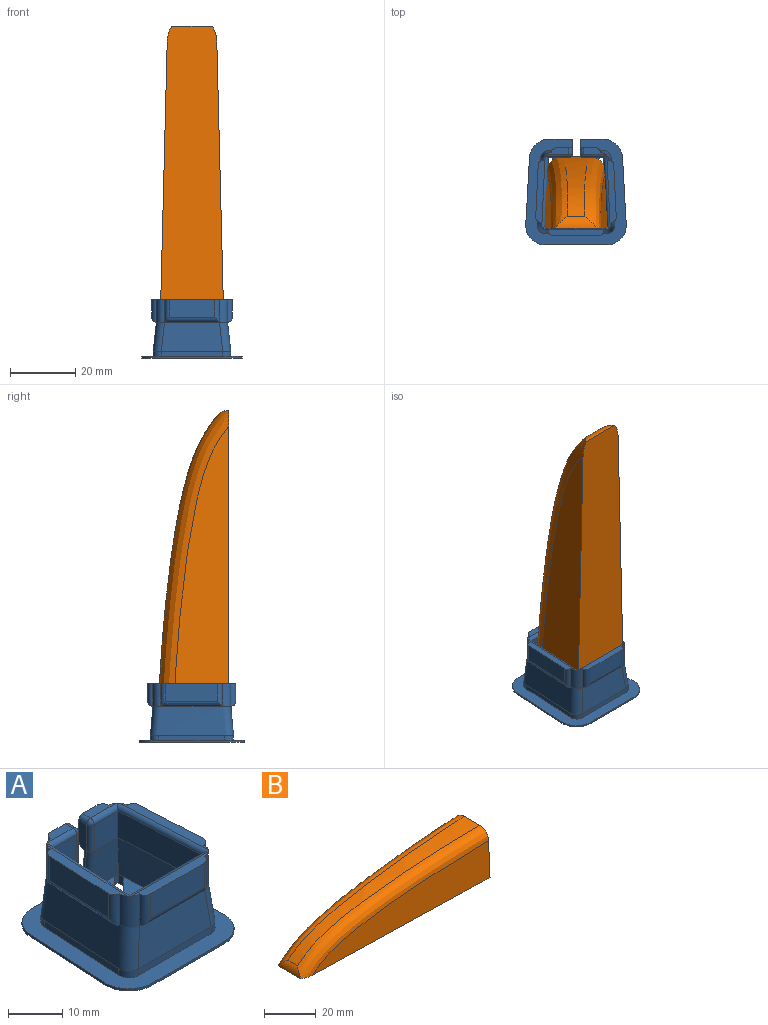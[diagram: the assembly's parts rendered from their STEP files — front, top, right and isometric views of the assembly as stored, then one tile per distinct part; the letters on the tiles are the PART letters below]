
ASSEMBLY  parts=2 mates=1
PART A: 109 faces, bbox 31x32.6x18.1 mm
  f0: plane 6.74x2mm, normal (0,0,1), area 10.5mm2, adj f11,f76,f82,f104,f108
  f1: plane 22x2.9mm, normal (0,0,1), area 38.1mm2, adj f71,f76,f81,f85,f87,f107
  f2: plane 6.85x2mm, normal (0,0,1), area 10.7mm2, adj f69,f78,f84,f97,f100
  f3: plane 22x2.9mm, normal (0,0,1), area 38.1mm2, adj f69,f70,f79,f88,f90,f102
  f4: plane 9.01x6.96mm, normal (0,-1,-0.08), area 59.3mm2, adj f6,f10,f20,f39,f101
  f5: plane 9.01x7.01mm, normal (0,1,0.08), area 59.8mm2, adj f7,f12,f19,f94
  f6: plane 7.07x5.34mm, normal (0,0,1), area 21.4mm2, adj f4,f8,f37,f38,f94,f101
  f7: plane 7.02x1.51mm, normal (0,1,0), area 10.5mm2, adj f5,f24,f68,f94
  f8: cylinder r=2.25mm len=2mm, axis (0,0,-1), area 0.9mm2, adj f6,f37,f59,f94
  f9: plane 7x0.5mm, normal (0,1,0), area 3.5mm2, adj f59,f67,f68,f94
  f10: plane 6.19x6mm, normal (0,-1,0), area 37.2mm2, adj f4,f75,f103,f108
  f11: plane 5.5x4.74mm, normal (0,1,0), area 25.9mm2, adj f0,f12,f82,f94,f104
  f12: cylinder r=1.5mm len=6.24mm, axis (-1,0,0), area 12.9mm2, adj f5,f11,f82,f94
  f13: bspline ~22.5x9mm, area 196.9mm2, adj f14,f18,f21,f32,f52,f73
  f14: plane 9.01x7.07mm, normal (0,-1,-0.08), area 60.3mm2, adj f13,f22,f33,f74,f96
  f15: plane 9.01x7.12mm, normal (0,1,0.08), area 60.8mm2, adj f16,f25,f83,f95
  f16: bspline ~25.5x9mm, area 250mm2, adj f15,f17,f26,f27,f28,f69,f70,f89
  f17: plane 18.9x9.01mm, normal (0,-1,0.09), area 161.7mm2, adj f16,f19,f29,f92
  f18: plane 21.01x9.01mm, normal (0,1,-0.09), area 180.7mm2, adj f13,f20,f23,f47,f51,f72
  f19: bspline ~25.5x9mm, area 250mm2, adj f5,f17,f24,f30,f57,f71,f76,f86
  f20: bspline ~22.5x9mm, area 196.9mm2, adj f4,f18,f40,f46,f58,f75
  f21: plane 20.13x7.07mm, normal (0,0,1), area 87.7mm2, adj f13,f31,f53,f54,f55,f56
  f22: plane 7.18x5.34mm, normal (0,0,1), area 21.8mm2, adj f14,f34,f35,f36,f95,f96
  f23: plane 18.97x4.85mm, normal (0,0,1), area 63.3mm2, adj f18,f48,f49,f50
  f24: cylinder r=2.5mm len=2.5mm, axis (0,0,-1), area 5.7mm2, adj f7,f19,f57,f68
  f25: plane 7.12x1.51mm, normal (0,1,0), area 10.7mm2, adj f15,f26,f68,f95
  f26: cylinder r=2.5mm len=2.5mm, axis (0,0,-1), area 5.7mm2, adj f16,f25,f27,f68
  f27: plane 20.59x1.59mm, normal (-1,0.06,0), area 30.8mm2, adj f16,f26,f28,f68
  f28: cylinder r=2.5mm len=2.64mm, axis (0,0,-1), area 6.1mm2, adj f16,f27,f29,f68
  f29: plane 18.9x1.51mm, normal (0,-1,0), area 28.3mm2, adj f17,f28,f30,f68
  f30: cylinder r=2.5mm len=2.64mm, axis (0,0,-1), area 6.1mm2, adj f19,f29,f57,f68
  f31: plane 4.46x4.36mm, normal (0.72,0.7,0), area 12.5mm2, adj f21,f32,f56,f59
  f32: plane 2.01x1.28mm, normal (1,-0.06,0), area 2.5mm2, adj f13,f31,f33,f59
  f33: plane 2.01x0.93mm, normal (0,-1,0), area 1.8mm2, adj f14,f32,f34,f59
  f34: plane 4.3x4.21mm, normal (-0.71,-0.7,0), area 12mm2, adj f22,f33,f35,f59
  f35: plane 2.51x2mm, normal (0,-1,0), area 5mm2, adj f22,f34,f36,f59
  f36: cylinder r=2.25mm len=2mm, axis (0,0,-1), area 1.1mm2, adj f22,f35,f59,f95
  f37: plane 2.51x2mm, normal (0,-1,0), area 5mm2, adj f6,f8,f38,f59
  f38: plane 4.3x4.21mm, normal (0.71,-0.7,0), area 12mm2, adj f6,f37,f39,f59
  f39: plane 2.01x0.93mm, normal (0,-1,0), area 1.8mm2, adj f4,f38,f40,f59
  f40: plane 2.01x1.28mm, normal (-1,-0.06,0), area 2.5mm2, adj f20,f39,f41,f59
  f41: plane 4.46x4.36mm, normal (-0.72,0.7,0), area 12.5mm2, adj f40,f42,f58,f59
  f42: plane 5.03x2mm, normal (-0.95,0.3,0), area 10.5mm2, adj f41,f43,f58,f59
  f43: plane 4.03x2mm, normal (-1,0,0), area 8.1mm2, adj f42,f44,f58,f59
  f44: plane 2x0.89mm, normal (-0.78,-0.63,0), area 2.3mm2, adj f43,f45,f58,f59
  f45: plane 6.35x5.72mm, normal (-0.67,-0.74,0), area 17.1mm2, adj f44,f46,f58,f59
  f46: plane 2.01x1.12mm, normal (-1,-0.06,0), area 2.2mm2, adj f20,f45,f47,f59
  f47: plane 2.01x1.03mm, normal (0,1,0), area 2mm2, adj f18,f46,f48,f59
  f48: plane 5.91x4.85mm, normal (0.63,0.77,0), area 15.3mm2, adj f23,f47,f49,f59
  f49: plane 7.15x2mm, normal (0,1,0), area 14.3mm2, adj f23,f48,f50,f59
  f50: plane 5.91x4.85mm, normal (-0.63,0.77,0), area 15.3mm2, adj f23,f49,f51,f59
  f51: plane 2.01x1.03mm, normal (0,1,0), area 2mm2, adj f18,f50,f52,f59
  f52: plane 2.01x1.12mm, normal (1,-0.06,0), area 2.2mm2, adj f13,f51,f53,f59
  f53: plane 6.35x5.72mm, normal (0.67,-0.74,0), area 17.1mm2, adj f21,f52,f54,f59
  f54: plane 2x0.89mm, normal (0.78,-0.63,0), area 2.3mm2, adj f21,f53,f55,f59
  f55: plane 4.03x2mm, normal (1,0,0), area 8.1mm2, adj f21,f54,f56,f59
  f56: plane 5.03x2mm, normal (0.95,0.3,0), area 10.5mm2, adj f21,f31,f55,f59
  f57: plane 20.59x1.59mm, normal (1,0.06,0), area 30.8mm2, adj f19,f24,f30,f68
  f58: plane 20.12x7.06mm, normal (0,0,1), area 87.4mm2, adj f20,f41,f42,f43,f44,f45
  f59: plane 32.5x30.89mm, normal (0,0,-1), area 760.5mm2, adj f8,f9,f31,f32,f33,f34,f35,f36
  f60: plane 7.11x0.5mm, normal (0,1,0), area 3.6mm2, adj f59,f61,f68,f95
  f61: cylinder r=6mm len=5.99mm, axis (0,0,-1), area 4.5mm2, adj f59,f60,f62,f68
  f62: plane 20.5x1.14mm, normal (-1,0.06,0), area 10.3mm2, adj f59,f61,f63,f68
  f63: cylinder r=6mm len=6.33mm, axis (0,0,-1), area 4.9mm2, adj f59,f62,f64,f68
  f64: plane 18.89x0.5mm, normal (0,-1,0), area 9.4mm2, adj f59,f63,f65,f68
  f65: cylinder r=6mm len=6.33mm, axis (0,0,-1), area 4.9mm2, adj f59,f64,f66,f68
  f66: plane 20.5x1.14mm, normal (1,0.06,0), area 10.3mm2, adj f59,f65,f67,f68
  f67: cylinder r=6mm len=5.99mm, axis (0,0,-1), area 4.5mm2, adj f9,f59,f66,f68
  f68: plane 32.5x30.89mm, normal (0,0,1), area 352.7mm2, adj f7,f9,f24,f25,f26,f27,f28,f29
  f69: cylinder r=2.5mm len=7mm, axis (0,0,1), area 26.7mm2, adj f2,f3,f16,f84,f88,f100,f102
  f70: cylinder r=2.5mm len=7mm, axis (0,0,1), area 28.3mm2, adj f3,f16,f77,f90,f91,f102,f105
  f71: cylinder r=2.5mm len=7mm, axis (0,0,1), area 28.3mm2, adj f1,f19,f77,f85,f93,f105,f107
  f72: plane 19x6mm, normal (0,1,0), area 114mm2, adj f18,f73,f75,f105
  f73: plane 21x6mm, normal (1,-0.05,0), area 126.1mm2, adj f13,f72,f74,f102
  f74: plane 6.31x6mm, normal (0,-1,0), area 37.8mm2, adj f14,f73,f98,f100
  f75: plane 21x6mm, normal (-1,-0.05,0), area 126.1mm2, adj f10,f20,f72,f107
  f76: cylinder r=2.5mm len=7mm, axis (0,0,1), area 26.7mm2, adj f0,f1,f19,f82,f87,f107,f108
  f77: plane 19.9x2mm, normal (0,0,1), area 33.9mm2, adj f70,f71,f80,f91,f93,f105
  f78: plane 5.5x4.85mm, normal (0,1,0), area 26.5mm2, adj f2,f83,f84,f95,f97
  f79: plane 16x5.5mm, normal (-1,0.05,0), area 88.1mm2, adj f3,f88,f89,f90
  f80: plane 13.9x5.5mm, normal (0,-1,0), area 76.5mm2, adj f77,f91,f92,f93
  f81: plane 16x5.5mm, normal (1,0.05,0), area 88.1mm2, adj f1,f85,f86,f87
  f82: cylinder r=1.5mm len=7mm, axis (0,0,-1), area 14.7mm2, adj f0,f11,f12,f76
  f83: cylinder r=1.5mm len=6.35mm, axis (-1,0,0), area 13.2mm2, adj f15,f78,f84,f95
  f84: cylinder r=1.5mm len=7mm, axis (0,0,1), area 14.7mm2, adj f2,f69,f78,f83
  f85: cylinder r=1.5mm len=7mm, axis (0,0,-1), area 14.7mm2, adj f1,f71,f81,f86
  f86: bspline ~19.07x2.4mm, area 41.3mm2, adj f19,f81,f85,f87
  f87: cylinder r=1.5mm len=7mm, axis (0,0,1), area 14.7mm2, adj f1,f76,f81,f86
  f88: cylinder r=1.5mm len=7mm, axis (0,0,-1), area 14.7mm2, adj f3,f69,f79,f89
  f89: bspline ~19.07x2.4mm, area 41.3mm2, adj f16,f79,f88,f90
  f90: cylinder r=1.5mm len=7mm, axis (0,0,1), area 14.7mm2, adj f3,f70,f79,f89
  f91: cylinder r=1.5mm len=7mm, axis (0,0,-1), area 14.7mm2, adj f70,f77,f80,f92
  f92: cylinder r=1.5mm len=16.9mm, axis (-1,0,0), area 36.3mm2, adj f17,f80,f91,f93
  f93: cylinder r=1.5mm len=7mm, axis (0,0,1), area 14.7mm2, adj f71,f77,f80,f92
  f94: plane 17x9.01mm, normal (-1,0,0), area 28.8mm2, adj f5,f6,f7,f8,f9,f11,f12,f59
  f95: plane 17x8.95mm, normal (1,0,0), area 28.6mm2, adj f15,f22,f25,f36,f59,f60,f68,f78
  f96: cylinder r=1mm len=9.16mm, axis (0,0.08,-1), area 14.2mm2, adj f14,f22,f95,f98
  f97: cylinder r=1mm len=2mm, axis (0,1,0), area 3.1mm2, adj f2,f78,f95,f99
  f98: cylinder r=1mm len=6mm, axis (0,0,1), area 9.4mm2, adj f74,f95,f96,f99
  f99: sphere r=1mm, area 1.6mm2, adj f97,f98,f100
  f100: cylinder r=1mm len=7.08mm, axis (1,0,0), area 10.4mm2, adj f2,f69,f74,f99,f102
  f101: cylinder r=1mm len=9.16mm, axis (0,-0.08,1), area 14.2mm2, adj f4,f6,f94,f103
  f102: cylinder r=1mm len=22.58mm, axis (0.05,1,0), area 34mm2, adj f3,f69,f70,f73,f100,f105
  f103: cylinder r=1mm len=6mm, axis (0,0,-1), area 9.4mm2, adj f10,f94,f101,f106
  f104: cylinder r=1mm len=2mm, axis (0,-1,0), area 3.1mm2, adj f0,f11,f94,f106
  f105: cylinder r=1mm len=20.52mm, axis (-1,0,0), area 31.2mm2, adj f70,f71,f72,f77,f102,f107
  f106: sphere r=1mm, area 1.6mm2, adj f103,f104,f108
  f107: cylinder r=1mm len=22.58mm, axis (0.05,-1,0), area 34mm2, adj f1,f71,f75,f76,f105,f108
  f108: cylinder r=1mm len=6.97mm, axis (1,0,0), area 10.2mm2, adj f0,f10,f76,f106,f107
PART B: 8 faces, bbox 103.8x20.2x25.8 mm
  f0: plane 95.06x17.24mm, normal (-0.02,-1,0.05), area 1188.2mm2, adj f2,f3,f5
  f1: extruded ~98.19x18.45mm, area 652.2mm2, adj f2,f5,f6,f7
  f2: plane 22.18x20.18mm, normal (1,0,0), area 408.4mm2, adj f0,f1,f3,f4,f5,f7
  f3: plane 100.19x20.19mm, normal (0,0,-1), area 1746.1mm2, adj f0,f2,f4,f5,f6,f7
  f4: plane 95.06x17.24mm, normal (-0.02,1,0.05), area 1188.2mm2, adj f2,f3,f7
  f5: bspline ~103.57x25.58mm, area 775.4mm2, adj f0,f1,f2,f3,f6
  f6: cylinder r=5mm len=12.47mm, axis (0,1,0), area 36.3mm2, adj f1,f3,f5,f7
  f7: bspline ~103.57x25.58mm, area 775.4mm2, adj f1,f2,f3,f4,f6
PLACE A t=(-3.01,54.95,-112.35)mm
PLACE B rot(axis=(-0.58,0.58,0.58),120deg) t=(-12.61,-14.73,-110.35)mm
MATE fastened B.f2 <-> A.f23  axis (0,0,-1) through (-2.61,-14.73,-110.35)mm
